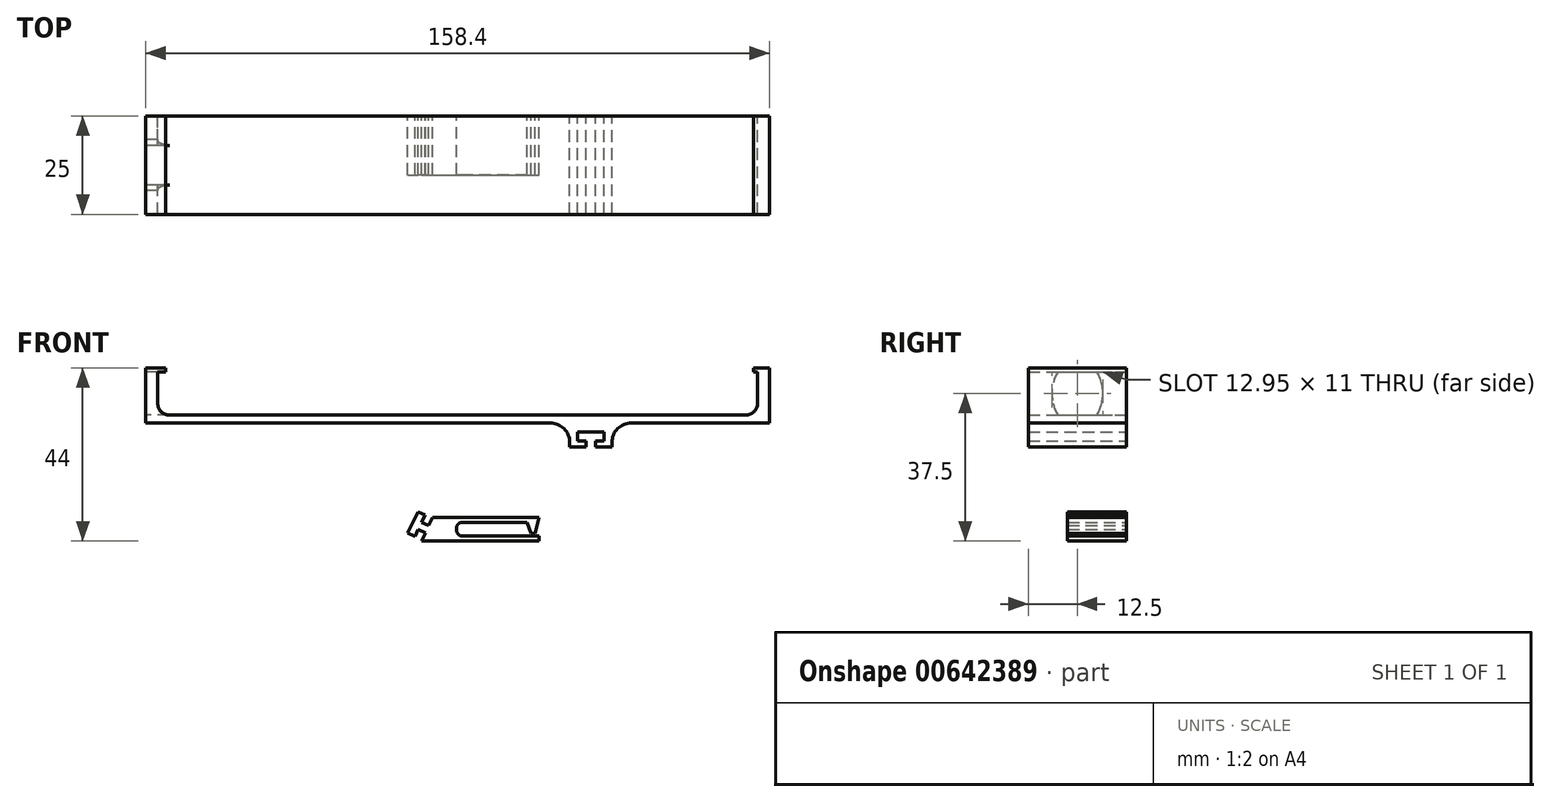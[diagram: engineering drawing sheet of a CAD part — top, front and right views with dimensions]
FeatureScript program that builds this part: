
annotation { "Feature Type Name" : "Feature", "Feature Type Description" : "" }
export const myFeature = defineFeature(function(context is Context, id is Id, definition is map)
    precondition{}
    {
        {
            var Q0;
            Q0=qCreatedBy(makeId("Front.planeOp"),FACE);
            var sketch = newSketch(context, id + "F0", { "sketchPlane" : qUnion([Q0])});
            skLineSegment(sketch, "E0.bottom", {"start": v(10, 0) * mm, "end": v(36.97, 0) * mm});
            skLineSegment(sketch, "E0.top", {"start": v(12.88, 6) * mm, "end": v(39.88, 6) * mm});
            skLineSegment(sketch, "E1", {"start": v(36.88, 4.75) * mm, "end": v(20.42, 4.75) * mm});
            skLineSegment(sketch, "E2", {"start": v(18.92, 3.21) * mm, "end": v(18.93, 2.7) * mm});
            skLineSegment(sketch, "E3", {"start": v(10, 0) * mm, "end": v(11, 2.1) * mm});
            skLineSegment(sketch, "E4.0", {"start": v(11.87, 3.9) * mm, "end": v(10.07, 4.77) * mm});
            skLineSegment(sketch, "E5.0", {"start": v(11, 2.1) * mm, "end": v(9.2, 2.97) * mm});
            skLineSegment(sketch, "E6.0", {"start": v(6.54, 2.03) * mm, "end": v(9.13, 7.44) * mm});
            skLineSegment(sketch, "E7.0", {"start": v(8.34, 1.16) * mm, "end": v(9.2, 2.97) * mm});
            skLineSegment(sketch, "E8", {"start": v(10.93, 6.57) * mm, "end": v(9.13, 7.44) * mm});
            skLineSegment(sketch, "E9", {"start": v(6.54, 2.03) * mm, "end": v(8.34, 1.16) * mm});
            skLineSegment(sketch, "E10.trimOffspring", {"start": v(10.07, 4.77) * mm, "end": v(10.93, 6.57) * mm});
            skLineSegment(sketch, "E11.trimOffspring", {"start": v(11.87, 3.9) * mm, "end": v(12.88, 6) * mm});
            skLineSegment(sketch, "E12.bottom", {"start": v(-60, 30) * mm, "end": v(42.7, 30) * mm});
            skLineSegment(sketch, "E12.top", {"start": v(-60, 44) * mm, "end": v(-55, 44) * mm});
            skLineSegment(sketch, "E12.left", {"start": v(-60, 30) * mm, "end": v(-60, 44) * mm});
            skLineSegment(sketch, "E12.right", {"start": v(98.4, 30) * mm, "end": v(98.4, 44) * mm});
            skLineSegment(sketch, "E13", {"start": v(-55, 44) * mm, "end": v(-55, 43) * mm});
            skLineSegment(sketch, "E14", {"start": v(-55, 43) * mm, "end": v(-57, 43) * mm});
            skLineSegment(sketch, "E15", {"start": v(-57, 43) * mm, "end": v(-57, 35) * mm});
            skLineSegment(sketch, "E16", {"start": v(-54, 32) * mm, "end": v(92.4, 32) * mm});
            skLineSegment(sketch, "E17", {"start": v(95.4, 35) * mm, "end": v(95.4, 43) * mm});
            skLineSegment(sketch, "E18", {"start": v(95.4, 43) * mm, "end": v(94.4, 43) * mm});
            skLineSegment(sketch, "E19", {"start": v(94.4, 43) * mm, "end": v(94.4, 44) * mm});
            skLineSegment(sketch, "E20.trimOffspring", {"start": v(94.4, 44) * mm, "end": v(98.4, 44) * mm});
            skLineSegment(sketch, "E21", {"start": v(47.7, 25) * mm, "end": v(47.7, 23.9) * mm});
            skLineSegment(sketch, "E22", {"start": v(47.7, 23.9) * mm, "end": v(51.8, 23.9) * mm});
            skLineSegment(sketch, "E23", {"start": v(51.8, 23.9) * mm, "end": v(51.8, 25.4) * mm});
            skLineSegment(sketch, "E24", {"start": v(51.8, 25.4) * mm, "end": v(49.7, 25.4) * mm});
            skLineSegment(sketch, "E25", {"start": v(49.7, 25.4) * mm, "end": v(49.7, 27.7) * mm});
            skLineSegment(sketch, "E26", {"start": v(49.7, 27.7) * mm, "end": v(56.4, 27.7) * mm});
            skLineSegment(sketch, "E27", {"start": v(56.4, 27.7) * mm, "end": v(56.4, 25.4) * mm});
            skLineSegment(sketch, "E28", {"start": v(56.4, 25.4) * mm, "end": v(54.3, 25.4) * mm});
            skLineSegment(sketch, "E29", {"start": v(54.3, 25.4) * mm, "end": v(54.3, 23.9) * mm});
            skLineSegment(sketch, "E30", {"start": v(54.3, 23.9) * mm, "end": v(58.4, 23.9) * mm});
            skLineSegment(sketch, "E31", {"start": v(58.4, 23.9) * mm, "end": v(58.4, 25) * mm});
            skLineSegment(sketch, "E32.trimOffspring", {"start": v(63.4, 30) * mm, "end": v(98.4, 30) * mm});
            skPoint(sketch, "E33.visualSharp", {"position": v(47.7, 30) * mm});
            skArc(sketch, "E33.filletArc", {"start": v(47.7, 25) * mm, "mid": v(46.24, 28.54) * mm, "end": v(42.7, 30) * mm});
            skPoint(sketch, "E34.visualSharp", {"position": v(58.4, 30) * mm});
            skArc(sketch, "E34.filletArc", {"start": v(63.4, 30) * mm, "mid": v(59.86, 28.54) * mm, "end": v(58.4, 25) * mm});
            skLineSegment(sketch, "E35", {"start": v(36.97, 0) * mm, "end": v(39.88, 0) * mm});
            skLineSegment(sketch, "E36", {"start": v(39.88, 0) * mm, "end": v(39.88, 1.24) * mm});
            skLineSegment(sketch, "E37", {"start": v(20.43, 1.25) * mm, "end": v(39.88, 1.24) * mm});
            skLineSegment(sketch, "E38", {"start": v(36.88, 4.75) * mm, "end": v(37.88, 1.93) * mm});
            skLineSegment(sketch, "E39", {"start": v(38.12, 1.24) * mm, "end": v(38.7, 1.24) * mm});
            skLineSegment(sketch, "E40", {"start": v(38.88, 1.93) * mm, "end": v(39.88, 6) * mm});
            skLineSegment(sketch, "E41", {"start": v(37.88, 1.93) * mm, "end": v(38.88, 1.93) * mm});
            skPoint(sketch, "E42.visualSharp", {"position": v(-57, 32) * mm});
            skArc(sketch, "E42.filletArc", {"start": v(-57, 35) * mm, "mid": v(-56.12, 32.88) * mm, "end": v(-54, 32) * mm});
            skPoint(sketch, "E43.visualSharp", {"position": v(95.4, 32) * mm});
            skArc(sketch, "E43.filletArc", {"start": v(92.4, 32) * mm, "mid": v(94.52, 32.88) * mm, "end": v(95.4, 35) * mm});
            skPoint(sketch, "E44.visualSharp", {"position": v(18.88, 4.75) * mm});
            skArc(sketch, "E44.filletArc", {"start": v(20.42, 4.75) * mm, "mid": v(19.34, 4.3) * mm, "end": v(18.92, 3.21) * mm});
            skPoint(sketch, "E45.visualSharp", {"position": v(18.97, 1.25) * mm});
            skArc(sketch, "E45.filletArc", {"start": v(18.93, 2.7) * mm, "mid": v(19.38, 1.67) * mm, "end": v(20.43, 1.25) * mm});
            skSolve(sketch);
        }
        {
            var Q0;
            Q0=makeQuery(id+"F0.imprint","IMPRINT",FACE,{"disambiguationData":[TD([[makeQuery(id+"F0.imprint","IMPRINT",EDGE,{"derivedFrom":sQuery(id+"F0.wireOp",EDGE,"E0.bottom")}),1.0]])]});
            extrude(context, id + "F1", {"entities" : qUnion([Q0]), "depth" : 15 * mm, "offsetDistance" : 25 * mm});
        }
        {
            var Q0;
            Q0=makeQuery(id+"F0.imprint","IMPRINT",FACE,{"disambiguationData":[TD([[makeQuery(id+"F0.imprint","IMPRINT",EDGE,{"derivedFrom":sQuery(id+"F0.wireOp",EDGE,"E12.bottom")}),1.0]])]});
            extrude(context, id + "F2", {"entities" : qUnion([Q0]), "depth" : 25 * mm, "offsetDistance" : 25 * mm});
        }
        {
            var Q0;
            Q0=makeQuery(id+"F2.opExtrude","SWEPT_FACE",FACE,{"disambiguationData":[OSD([sQuery(id+"F0.wireOp",EDGE,"E12.left")])]});
            var sketch = newSketch(context, id + "F3", { "sketchPlane" : qUnion([Q0])});
            skLineSegment(sketch, "E46.0", {"start": v(17.5, 32) * mm, "end": v(7.5, 32) * mm});
            skLineSegment(sketch, "E46.1", {"start": v(17.5, 43) * mm, "end": v(7.5, 43) * mm});
            skLineSegment(sketch, "E47.0", {"start": v(17.5, 32) * mm, "end": v(17.5, 43) * mm, "construction": true});
            skLineSegment(sketch, "E48.0", {"start": v(7.5, 32) * mm, "end": v(7.5, 43) * mm, "construction": true});
            skArc(sketch, "E49", {"start": v(7.5, 43) * mm, "mid": v(6.03, 37.5) * mm, "end": v(7.5, 32) * mm});
            skArc(sketch, "E50", {"start": v(17.5, 32) * mm, "mid": v(18.97, 37.5) * mm, "end": v(17.5, 43) * mm});
            skSolve(sketch);
        }
        {
            var Q0;
            Q0=makeQuery(id+"F3.imprint","IMPRINT",FACE,{"disambiguationData":[TD([[makeQuery(id+"F3.imprint","IMPRINT",EDGE,{"derivedFrom":sQuery(id+"F3.wireOp",EDGE,"E46.0")}),-1.0]])]});
            extrude(context, id + "F4", {"entities" : qUnion([Q0]), "operationType" : NewBodyOperationType.REMOVE, "oppositeDirection" : true, "depth" : 6 * mm, "offsetDistance" : 25 * mm});
        }
    });
